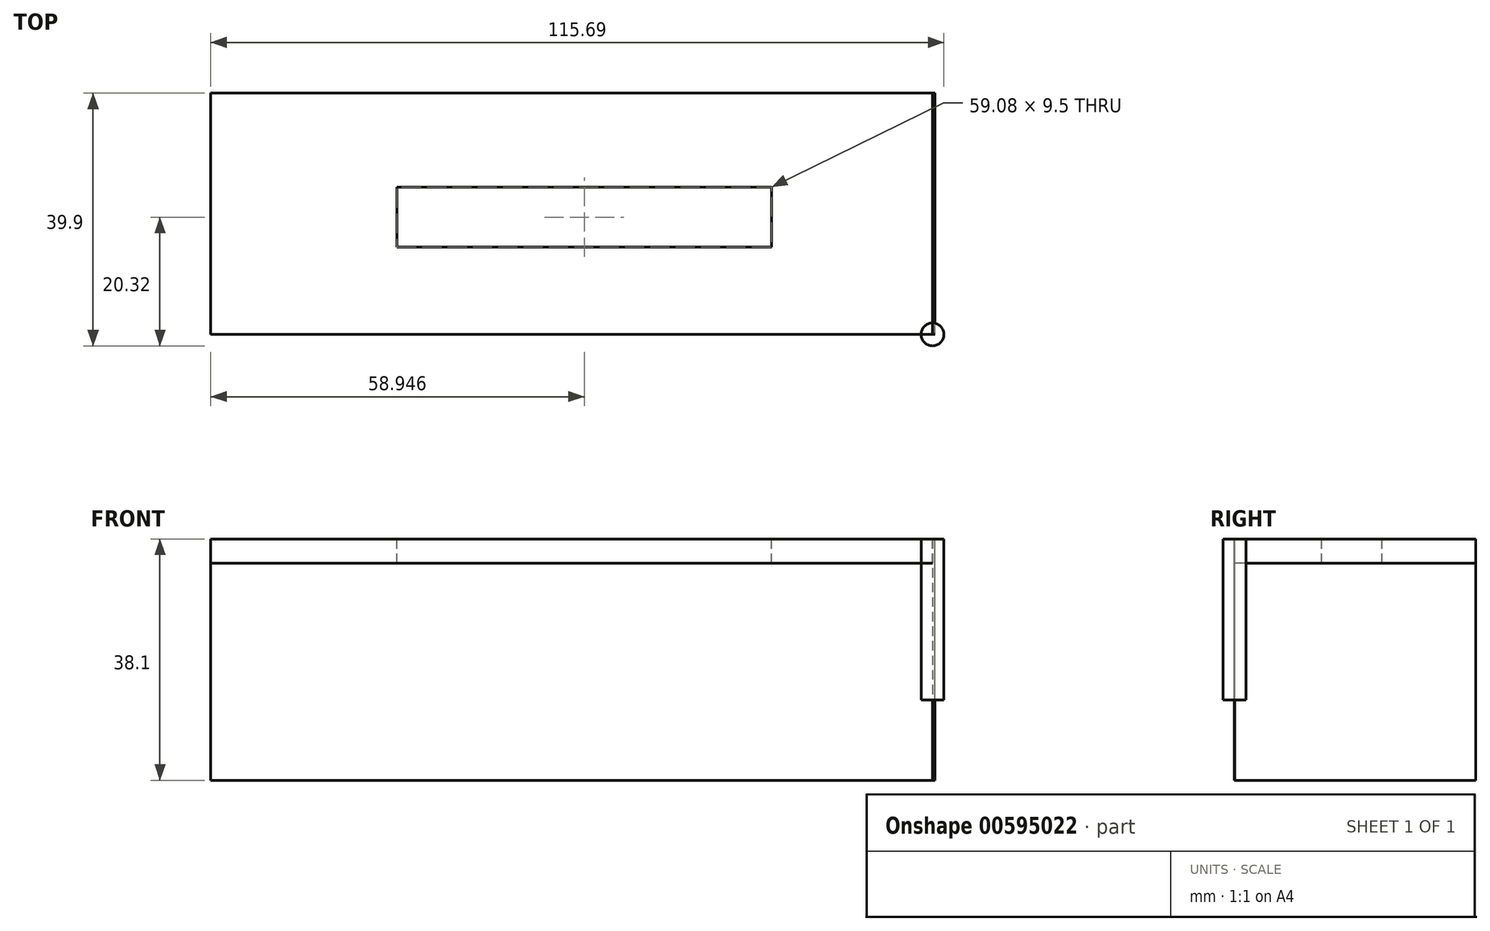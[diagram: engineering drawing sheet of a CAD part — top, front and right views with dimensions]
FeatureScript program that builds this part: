
annotation { "Feature Type Name" : "Feature", "Feature Type Description" : "" }
export const myFeature = defineFeature(function(context is Context, id is Id, definition is map)
    precondition{}
    {
        {
            var Q0;
            Q0=qCreatedBy(makeId("Top.planeOp"),FACE);
            var sketch = newSketch(context, id + "F0", { "sketchPlane" : qUnion([Q0])});
            skLineSegment(sketch, "E0.bottom", {"start": v(0, 0) * mm, "end": v(114.3, 0) * mm});
            skLineSegment(sketch, "E0.top", {"start": v(0, 38.1) * mm, "end": v(114.3, 38.1) * mm});
            skLineSegment(sketch, "E0.left", {"start": v(0, 0) * mm, "end": v(0, 38.1) * mm});
            skLineSegment(sketch, "E0.right", {"start": v(114.3, 0) * mm, "end": v(114.3, 38.1) * mm});
            skSolve(sketch);
        }
        {
            var Q0;
            Q0=makeQuery(id+"F0.imprint","IMPRINT",FACE,{"disambiguationData":[TD([[makeQuery(id+"F0.imprint","IMPRINT",EDGE,{"derivedFrom":sQuery(id+"F0.wireOp",EDGE,"E0.bottom")}),1.0]])]});
            extrude(context, id + "F1", {"entities" : qUnion([Q0]), "depth" : 1 / 203.2 * mm, "offsetDistance" : 25.4 * mm});
        }
        {
            var Q0;
            Q0=makeQuery(id+"F1.opExtrude","SWEPT_FACE",FACE,{"disambiguationData":[OSD([sQuery(id+"F0.wireOp",EDGE,"E0.bottom")])]});
            var sketch = newSketch(context, id + "F2", { "sketchPlane" : qUnion([Q0])});
            skLineSegment(sketch, "E1.bottom", {"start": v(0, 0) * mm, "end": v(114.3, 0) * mm});
            skLineSegment(sketch, "E1.top", {"start": v(0, 38.1) * mm, "end": v(114.3, 38.1) * mm});
            skLineSegment(sketch, "E1.left", {"start": v(0, 0) * mm, "end": v(0, 38.1) * mm});
            skLineSegment(sketch, "E1.right", {"start": v(114.3, 0) * mm, "end": v(114.3, 38.1) * mm});
            skSolve(sketch);
        }
        {
            var Q0;
            {var subQ0=sQuery(id+"F2.wireOp",EDGE,"E1.top");Q0=makeQuery(id+"F2.imprint","IMPRINT",FACE,{"disambiguationData":[TD([[makeQuery(id+"F2.imprint","IMPRINT",EDGE,{"derivedFrom":subQ0}),-1.0]])]});}
            extrude(context, id + "F3", {"entities" : qUnion([Q0]), "oppositeDirection" : true, "depth" : 1 / 203.2 * mm, "offsetDistance" : 25.4 * mm});
        }
        {
            var Q0;
            Q0=makeQuery(id+"F1.opExtrude","CAP_EDGE",EDGE,{"disambiguationData":[OSD([sQuery(id+"F0.wireOp",EDGE,"E0.top")])],"isStart":false});
            cPoint(context, id + "F4", {"entities" : qUnion([Q0]), "parameter" : 0.5});
        }
        {
            var Q0;
            Q0=makeQuery(id+"F1.opExtrude","CAP_EDGE",EDGE,{"disambiguationData":[OSD([sQuery(id+"F0.wireOp",EDGE,"E0.bottom")])],"isStart":false});
            cPoint(context, id + "F5", {"entities" : qUnion([Q0]), "parameter" : 0.5});
        }
        {
            var Q0;
            Q0 = qCreatedBy(id + "F4" ,VERTEX);
            var Q1;
            Q1 = qCreatedBy(id + "F5" ,VERTEX);
            cPlane(context, id + "F6", {"entities" : qUnion([Q0, Q1]), "cplaneType" : CPlaneType.MID_PLANE, "offset" : 25.4 * mm, "width" : 152.4 * mm, "height" : 152.4 * mm});
        }
        {
            var Q0;
            Q0=makeQuery(id+"F3.opExtrude","SWEPT_BODY",BODY,{"disambiguationData":[OSD([sQuery(id+"F0.wireOp",EDGE,"E0.bottom"),sQuery(id+"F2.wireOp",EDGE,"E1.top"),sQuery(id+"F2.wireOp",EDGE,"E1.left"),sQuery(id+"F2.wireOp",EDGE,"E1.right")])]});
            var Q1;
            Q1=qCreatedBy(id+"F6.planeOp",FACE);
            mirror(context, id + "F7", {"entities" : qUnion([Q0]), "mirrorPlane" : qUnion([Q1])});
        }
        {
            var Q0;
            Q0=makeQuery(id+"F7.opPattern","COPY",FACE,{"derivedFrom":makeQuery(id+"F3.opExtrude","SWEPT_FACE",FACE,{"disambiguationData":[OSD([sQuery(id+"F2.wireOp",EDGE,"E1.top")])]}),"instanceName":"1"});
            var sketch = newSketch(context, id + "F8", { "sketchPlane" : qUnion([Q0])});
            skLineSegment(sketch, "E2.bottom", {"start": v(0, 38.1) * mm, "end": v(113.89, 38.1) * mm});
            skLineSegment(sketch, "E2.top", {"start": v(0, 0) * mm, "end": v(113.89, 0) * mm});
            skLineSegment(sketch, "E2.left", {"start": v(0, 38.1) * mm, "end": v(0, 0) * mm});
            skLineSegment(sketch, "E2.right", {"start": v(113.89, 38.1) * mm, "end": v(113.89, 0) * mm});
            skLineSegment(sketch, "E3.bottom", {"start": v(29.4, 13.77) * mm, "end": v(88.49, 13.77) * mm});
            skLineSegment(sketch, "E3.top", {"start": v(29.4, 23.27) * mm, "end": v(88.49, 23.27) * mm});
            skLineSegment(sketch, "E3.left", {"start": v(29.4, 13.77) * mm, "end": v(29.4, 23.27) * mm});
            skLineSegment(sketch, "E3.right", {"start": v(88.49, 13.77) * mm, "end": v(88.49, 23.27) * mm});
            skLineSegment(sketch, "E4", {"start": v(0, 19.05) * mm, "end": v(113.89, 19.05) * mm});
            skLineSegment(sketch, "E5", {"start": v(4, 19.05) * mm, "end": v(29.4, 19.05) * mm});
            skLineSegment(sketch, "E6", {"start": v(88.49, 19.05) * mm, "end": v(113.89, 19.05) * mm});
            skSolve(sketch);
        }
        {
            var Q0;
            {var subQ0=sQuery(id+"F8.wireOp",EDGE,"E2.top");Q0=makeQuery(id+"F8.imprint","IMPRINT",FACE,{"disambiguationData":[TD([[makeQuery(id+"F8.imprint","IMPRINT",EDGE,{"derivedFrom":subQ0}),1.0]])]});}
            var Q1;
            {var subQ0=sQuery(id+"F8.wireOp",EDGE,"E2.bottom");Q1=makeQuery(id+"F8.imprint","IMPRINT",FACE,{"disambiguationData":[TD([[makeQuery(id+"F8.imprint","IMPRINT",EDGE,{"derivedFrom":subQ0}),-1.0]])]});}
            var Q2;
            {var subQ0=sQuery(id+"F8.wireOp",EDGE,"E3.top");Q2=makeQuery(id+"F8.imprint","IMPRINT",FACE,{"disambiguationData":[TD([[makeQuery(id+"F8.imprint","IMPRINT",EDGE,{"derivedFrom":subQ0}),1.0]])]});}
            extrude(context, id + "F9", {"entities" : qUnion([Q0, Q1, Q2]), "oppositeDirection" : true, "depth" : 3.8 * mm, "offsetDistance" : 25.4 * mm});
        }
        {
            var Q0;
            Q0=makeQuery(id+"F7.opPattern","COPY",FACE,{"derivedFrom":makeQuery(id+"F3.opExtrude","SWEPT_FACE",FACE,{"disambiguationData":[OSD([sQuery(id+"F2.wireOp",EDGE,"E1.left")])]}),"instanceName":"1"});
            var sketch = newSketch(context, id + "F10", { "sketchPlane" : qUnion([Q0])});
            skLineSegment(sketch, "E7.bottom", {"start": v(-38.1, 38.1) * mm, "end": v(0, 38.1) * mm});
            skLineSegment(sketch, "E7.top", {"start": v(-38.1, 0) * mm, "end": v(0, 0) * mm});
            skLineSegment(sketch, "E7.left", {"start": v(-38.1, 38.1) * mm, "end": v(-38.1, 0) * mm});
            skLineSegment(sketch, "E7.right", {"start": v(0, 38.1) * mm, "end": v(0, 0) * mm});
            skSolve(sketch);
        }
        {
            var Q0;
            Q0 = qSketchRegion(id + "F10", true);
            extrude(context, id + "F11", {"entities" : qUnion([Q0]), "oppositeDirection" : true, "depth" : 1 / 203.2 * mm, "offsetDistance" : 25.4 * mm});
        }
        {
            var Q0;
            Q0=makeQuery(id+"F9.opExtrude","SWEPT_FACE",FACE,{"disambiguationData":[OSD([sQuery(id+"F8.wireOp",EDGE,"E2.right")])]});
            var sketch = newSketch(context, id + "F12", { "sketchPlane" : qUnion([Q0])});
            skLineSegment(sketch, "E8.bottom", {"start": v(0, 38.1) * mm, "end": v(38.08, 38.1) * mm});
            skLineSegment(sketch, "E8.top", {"start": v(0, 0) * mm, "end": v(38.08, 0) * mm});
            skLineSegment(sketch, "E8.left", {"start": v(0, 38.1) * mm, "end": v(0, 0) * mm});
            skLineSegment(sketch, "E8.right", {"start": v(38.08, 38.1) * mm, "end": v(38.08, 0) * mm});
            skSolve(sketch);
        }
        {
            var Q0;
            Q0 = qSketchRegion(id + "F12", true);
            extrude(context, id + "F13", {"entities" : qUnion([Q0]), "oppositeDirection" : true, "depth" : 1 / 203.2 * mm, "offsetDistance" : 25.4 * mm});
        }
        {
            var Q0;
            {var subQ0=sQuery(id+"F8.wireOp",EDGE,"E3.top");Q0=makeQuery(id+"F8.imprint","IMPRINT",FACE,{"disambiguationData":[TD([[makeQuery(id+"F8.imprint","IMPRINT",EDGE,{"derivedFrom":subQ0}),-1.0]])]});}
            var Q1;
            {var subQ0=sQuery(id+"F8.wireOp",EDGE,"E3.bottom");Q1=makeQuery(id+"F8.imprint","IMPRINT",FACE,{"disambiguationData":[TD([[makeQuery(id+"F8.imprint","IMPRINT",EDGE,{"derivedFrom":subQ0}),1.0]])]});}
            extrude(context, id + "F14", {"entities" : qUnion([Q0, Q1]), "operationType" : NewBodyOperationType.REMOVE, "oppositeDirection" : true, "depth" : 1 / 203.2 * mm, "offsetDistance" : 25.4 * mm});
        }
        {
            var Q0;
            Q0=makeQuery(id+"F9.opExtrude","CAP_FACE",FACE,{"disambiguationData":[OSD([sQuery(id+"F8.wireOp",EDGE,"E2.bottom"),sQuery(id+"F8.wireOp",EDGE,"E2.top"),sQuery(id+"F8.wireOp",EDGE,"E2.left"),sQuery(id+"F8.wireOp",EDGE,"E2.right"),sQuery(id+"F8.wireOp",EDGE,"E3.bottom"),sQuery(id+"F8.wireOp",EDGE,"E3.top"),sQuery(id+"F8.wireOp",EDGE,"E3.left"),sQuery(id+"F8.wireOp",EDGE,"E3.right")])],"isStart":true});
            var sketch = newSketch(context, id + "F15", { "sketchPlane" : qUnion([Q0])});
            skCircle(sketch, "E9", {"center": v(113.89, 0) * mm, "radius": 1.8 * mm});
            skSolve(sketch);
        }
        {
            var Q0;
            Q0 = qSketchRegion(id + "F15", true);
            extrude(context, id + "F16", {"entities" : qUnion([Q0]), "oppositeDirection" : true, "depth" : 25.4 * mm, "offsetDistance" : 25.4 * mm});
        }
    });
